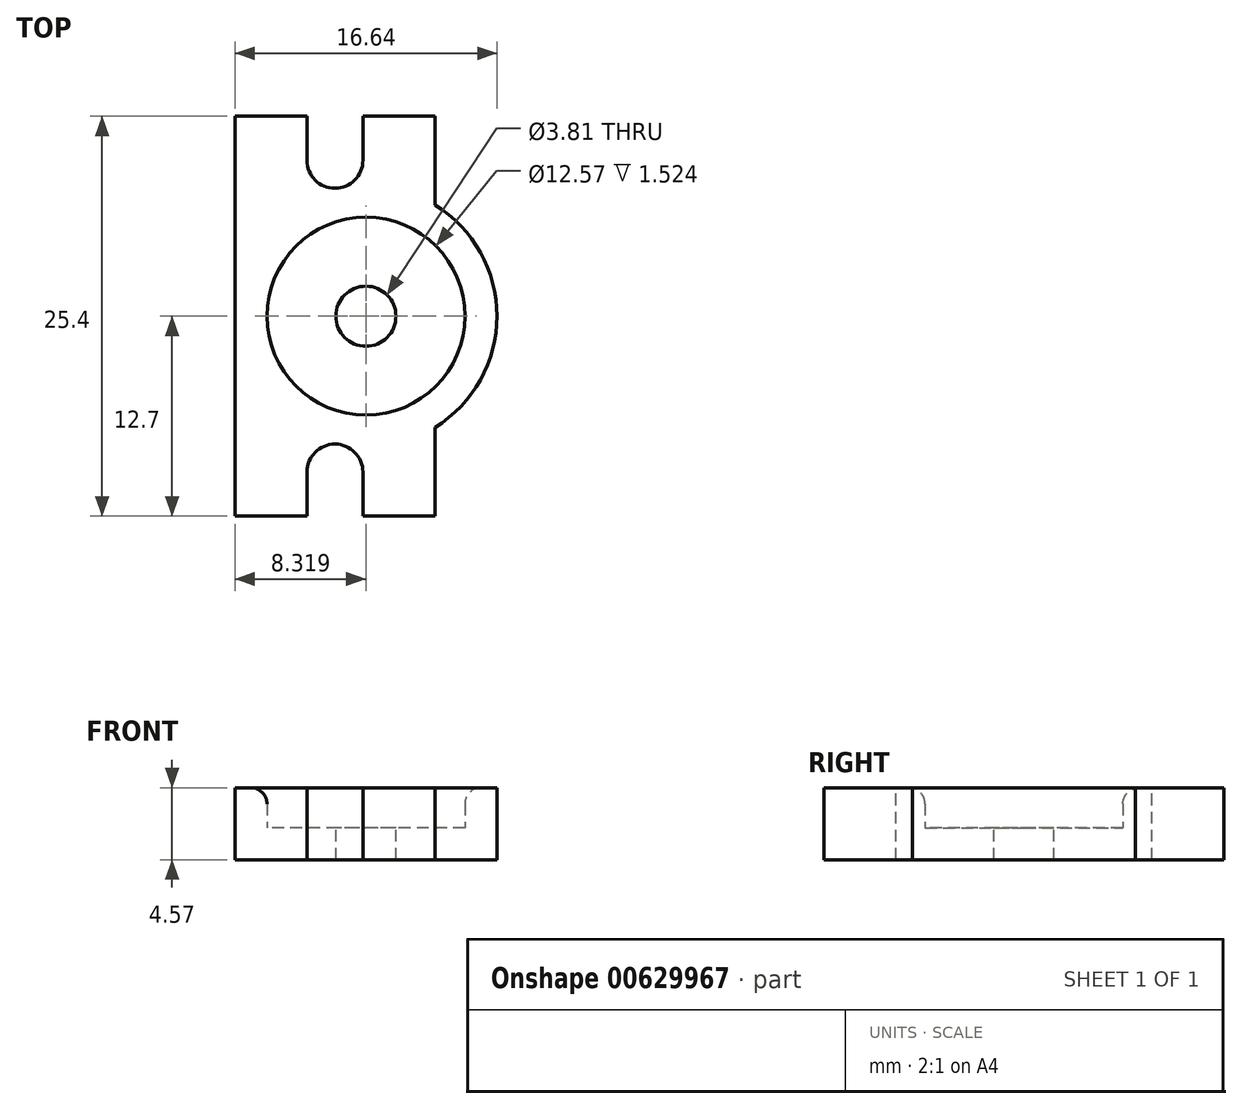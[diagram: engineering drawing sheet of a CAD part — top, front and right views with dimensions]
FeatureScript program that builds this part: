
annotation { "Feature Type Name" : "Feature", "Feature Type Description" : "" }
export const myFeature = defineFeature(function(context is Context, id is Id, definition is map)
    precondition{}
    {
        {
            var Q0;
            Q0=qCreatedBy(makeId("Top.planeOp"),FACE);
            var sketch = newSketch(context, id + "F0", { "sketchPlane" : qUnion([Q0])});
            skLineSegment(sketch, "E0.bottom", {"start": v(6.35, 12.7) * mm, "end": v(-6.35, 12.7) * mm});
            skLineSegment(sketch, "E0.top", {"start": v(6.35, -12.7) * mm, "end": v(-6.35, -12.7) * mm});
            skLineSegment(sketch, "E0.left", {"start": v(6.35, 12.7) * mm, "end": v(6.35, -12.7) * mm});
            skLineSegment(sketch, "E0.right", {"start": v(-6.35, 12.7) * mm, "end": v(-6.35, -12.7) * mm});
            skPoint(sketch, "E0.middle", {"position": v(0, 0) * mm});
            skCircle(sketch, "E1", {"center": v(1.97, 0) * mm, "radius": 6.29 * mm});
            skCircle(sketch, "E2", {"center": v(0, 9.9) * mm, "radius": 1.78 * mm});
            skCircle(sketch, "E3.MirrorC", {"center": v(0, -9.9) * mm, "radius": 1.78 * mm});
            skCircle(sketch, "E4", {"center": v(1.97, 0) * mm, "radius": 8.32 * mm});
            skLineSegment(sketch, "E5", {"start": v(-1.78, 9.9) * mm, "end": v(-1.78, 12.7) * mm});
            skLineSegment(sketch, "E6.MirrorCS", {"start": v(1.78, 9.9) * mm, "end": v(1.78, 12.7) * mm});
            skLineSegment(sketch, "E7.MirrorCS", {"start": v(-1.78, -9.9) * mm, "end": v(-1.78, -12.7) * mm});
            skLineSegment(sketch, "E8.MirrorCS", {"start": v(1.78, -9.9) * mm, "end": v(1.78, -12.7) * mm});
            skCircle(sketch, "E9", {"center": v(1.97, 0) * mm, "radius": 1.9 * mm});
            skSolve(sketch);
        }
        {
            var Q0;
            {var subQ1=sQuery(id+"F0.wireOp",EDGE,"E0.left");var subQ4=sQuery(id+"F0.wireOp",EDGE,"E4");var subQ7=makeQuery(id+"F0.imprint","INTERSECT",VERTEX,{"disambiguationData":[OD(0.0)],"derivedFrom":[subQ1,subQ4]});Q0=makeQuery(id+"F0.imprint","IMPRINT",FACE,{"disambiguationData":[TD([[makeQuery(id+"F0.imprint","IMPRINT",EDGE,{"disambiguationData":[TD([[subQ7,-1.0]])],"derivedFrom":subQ1}),-1.0]])]});}
            var Q1;
            {var subQ0=sQuery(id+"F0.wireOp",EDGE,"E1");var subQ1=sQuery(id+"F0.wireOp",EDGE,"E0.left");var subQ2=makeQuery(id+"F0.imprint","INTERSECT",VERTEX,{"disambiguationData":[OD(0.0)],"derivedFrom":[subQ1,subQ0]});Q1=makeQuery(id+"F0.imprint","IMPRINT",FACE,{"disambiguationData":[TD([[makeQuery(id+"F0.imprint","IMPRINT",EDGE,{"disambiguationData":[TD([[subQ2,-1.0]])],"derivedFrom":subQ1}),-1.0]])]});}
            var Q2;
            {var subQ0=sQuery(id+"F0.wireOp",EDGE,"E1");var subQ1=sQuery(id+"F0.wireOp",EDGE,"E0.left");var subQ2=makeQuery(id+"F0.imprint","INTERSECT",VERTEX,{"disambiguationData":[OD(0.0)],"derivedFrom":[subQ1,subQ0]});Q2=makeQuery(id+"F0.imprint","IMPRINT",FACE,{"disambiguationData":[TD([[makeQuery(id+"F0.imprint","IMPRINT",EDGE,{"disambiguationData":[TD([[subQ2,-1.0]])],"derivedFrom":subQ1}),1.0]])]});}
            var Q3;
            {var subQ0=sQuery(id+"F0.wireOp",EDGE,"E4");var subQ1=sQuery(id+"F0.wireOp",EDGE,"E0.left");var subQ2=makeQuery(id+"F0.imprint","INTERSECT",VERTEX,{"disambiguationData":[OD(0.0)],"derivedFrom":[subQ1,subQ0]});Q3=makeQuery(id+"F0.imprint","IMPRINT",FACE,{"disambiguationData":[TD([[makeQuery(id+"F0.imprint","IMPRINT",EDGE,{"disambiguationData":[TD([[subQ2,-1.0]])],"derivedFrom":subQ1}),1.0]])]});}
            var Q4;
            {var subQ0=sQuery(id+"F0.wireOp",EDGE,"E5");Q4=makeQuery(id+"F0.imprint","IMPRINT",FACE,{"disambiguationData":[TD([[makeQuery(id+"F0.imprint","IMPRINT",EDGE,{"derivedFrom":subQ0}),1.0]])]});}
            var Q5;
            {var subQ0=sQuery(id+"F0.wireOp",EDGE,"E6.MirrorCS");Q5=makeQuery(id+"F0.imprint","IMPRINT",FACE,{"disambiguationData":[TD([[makeQuery(id+"F0.imprint","IMPRINT",EDGE,{"derivedFrom":subQ0}),-1.0]])]});}
            var Q6;
            {var subQ5=sQuery(id+"F0.wireOp",EDGE,"E8.MirrorCS");Q6=makeQuery(id+"F0.imprint","IMPRINT",FACE,{"disambiguationData":[TD([[makeQuery(id+"F0.imprint","IMPRINT",EDGE,{"derivedFrom":subQ5}),1.0]])]});}
            var Q7;
            {var subQ7=sQuery(id+"F0.wireOp",EDGE,"E7.MirrorCS");Q7=makeQuery(id+"F0.imprint","IMPRINT",FACE,{"disambiguationData":[TD([[makeQuery(id+"F0.imprint","IMPRINT",EDGE,{"derivedFrom":subQ7}),-1.0]])]});}
            extrude(context, id + "F1", {"entities" : qUnion([Q0, Q1, Q2, Q3, Q4, Q5, Q6, Q7]), "oppositeDirection" : true, "depth" : 2.03 * mm, "offsetDistance" : 25.4 * mm});
        }
        {
            var Q0;
            {var subQ1=sQuery(id+"F0.wireOp",EDGE,"E0.left");var subQ4=sQuery(id+"F0.wireOp",EDGE,"E4");var subQ7=makeQuery(id+"F0.imprint","INTERSECT",VERTEX,{"disambiguationData":[OD(0.0)],"derivedFrom":[subQ1,subQ4]});Q0=makeQuery(id+"F0.imprint","IMPRINT",FACE,{"disambiguationData":[TD([[makeQuery(id+"F0.imprint","IMPRINT",EDGE,{"disambiguationData":[TD([[subQ7,-1.0]])],"derivedFrom":subQ1}),-1.0]])]});}
            var Q1;
            {var subQ0=sQuery(id+"F0.wireOp",EDGE,"E4");var subQ1=sQuery(id+"F0.wireOp",EDGE,"E0.left");var subQ2=makeQuery(id+"F0.imprint","INTERSECT",VERTEX,{"disambiguationData":[OD(0.0)],"derivedFrom":[subQ1,subQ0]});Q1=makeQuery(id+"F0.imprint","IMPRINT",FACE,{"disambiguationData":[TD([[makeQuery(id+"F0.imprint","IMPRINT",EDGE,{"disambiguationData":[TD([[subQ2,-1.0]])],"derivedFrom":subQ1}),1.0]])]});}
            var Q2;
            {var subQ0=sQuery(id+"F0.wireOp",EDGE,"E6.MirrorCS");Q2=makeQuery(id+"F0.imprint","IMPRINT",FACE,{"disambiguationData":[TD([[makeQuery(id+"F0.imprint","IMPRINT",EDGE,{"derivedFrom":subQ0}),-1.0]])]});}
            var Q3;
            {var subQ0=sQuery(id+"F0.wireOp",EDGE,"E5");Q3=makeQuery(id+"F0.imprint","IMPRINT",FACE,{"disambiguationData":[TD([[makeQuery(id+"F0.imprint","IMPRINT",EDGE,{"derivedFrom":subQ0}),1.0]])]});}
            var Q4;
            {var subQ5=sQuery(id+"F0.wireOp",EDGE,"E8.MirrorCS");Q4=makeQuery(id+"F0.imprint","IMPRINT",FACE,{"disambiguationData":[TD([[makeQuery(id+"F0.imprint","IMPRINT",EDGE,{"derivedFrom":subQ5}),1.0]])]});}
            var Q5;
            {var subQ7=sQuery(id+"F0.wireOp",EDGE,"E7.MirrorCS");Q5=makeQuery(id+"F0.imprint","IMPRINT",FACE,{"disambiguationData":[TD([[makeQuery(id+"F0.imprint","IMPRINT",EDGE,{"derivedFrom":subQ7}),-1.0]])]});}
            extrude(context, id + "F2", {"entities" : qUnion([Q0, Q1, Q2, Q3, Q4, Q5]), "operationType" : NewBodyOperationType.ADD, "depth" : 2.54 * mm, "offsetDistance" : 25.4 * mm});
        }
        {
            var Q0;
            Q0=makeQuery(id+"F2.opExtrude","CAP_EDGE",EDGE,{"disambiguationData":[OSD([sQuery(id+"F0.wireOp",EDGE,"E1")])],"isStart":false});
            fillet(context, id + "F3", {"entities" : qUnion([Q0]), "radius" : 1.02 * mm, "tangentPropagation" : true, "allowEdgeOverflow" : false});
        }
    });
